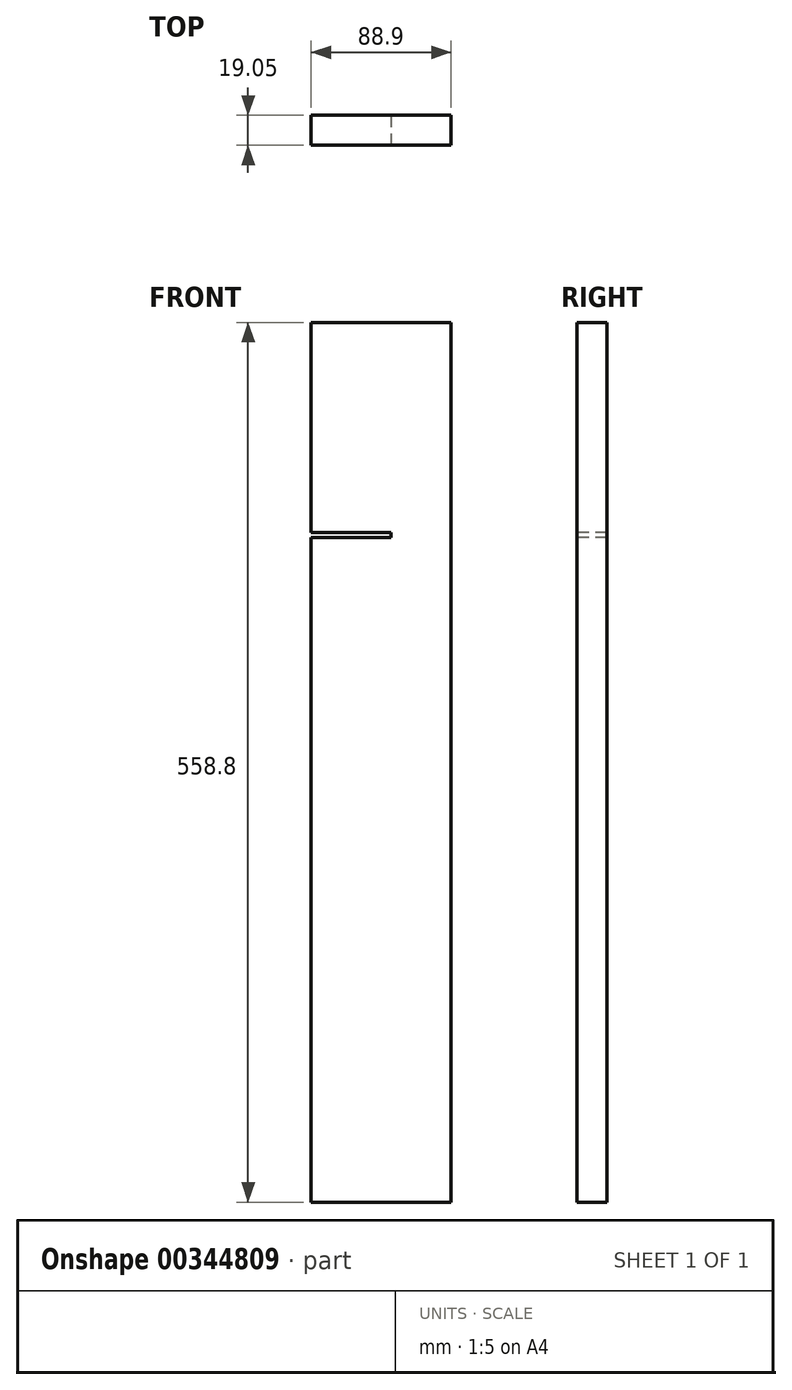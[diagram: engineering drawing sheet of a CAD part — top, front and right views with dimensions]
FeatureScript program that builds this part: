
annotation { "Feature Type Name" : "Feature", "Feature Type Description" : "" }
export const myFeature = defineFeature(function(context is Context, id is Id, definition is map)
    precondition{}
    {
        {
            var Q0;
            Q0=qCreatedBy(makeId("Front.planeOp"),FACE);
            var sketch = newSketch(context, id + "F0", { "sketchPlane" : qUnion([Q0])});
            skLineSegment(sketch, "E0.bottom", {"start": v(0, 0) * mm, "end": v(88.9, 0) * mm});
            skLineSegment(sketch, "E0.top", {"start": v(0, 558.8) * mm, "end": v(88.9, 558.8) * mm});
            skLineSegment(sketch, "E0.left", {"start": v(0, 0) * mm, "end": v(0, 558.8) * mm});
            skLineSegment(sketch, "E0.right", {"start": v(88.9, 0) * mm, "end": v(88.9, 558.8) * mm});
            skSolve(sketch);
        }
        {
            var Q0;
            Q0=makeQuery(id+"F0.imprint","IMPRINT",FACE,{"disambiguationData":[TD([[makeQuery(id+"F0.imprint","IMPRINT",EDGE,{"derivedFrom":sQuery(id+"F0.wireOp",EDGE,"E0.bottom")}),1.0]])]});
            extrude(context, id + "F1", {"entities" : qUnion([Q0]), "depth" : 19.05 * mm});
        }
        {
            var Q0;
            Q0=makeQuery(id+"F1.opExtrude","CAP_FACE",FACE,{"disambiguationData":[OSD([sQuery(id+"F0.wireOp",EDGE,"E0.bottom"),sQuery(id+"F0.wireOp",EDGE,"E0.top"),sQuery(id+"F0.wireOp",EDGE,"E0.left"),sQuery(id+"F0.wireOp",EDGE,"E0.right")])],"isStart":false});
            var sketch = newSketch(context, id + "F2", { "sketchPlane" : qUnion([Q0])});
            skLineSegment(sketch, "E1", {"start": v(0, 422.28) * mm, "end": v(88.9, 422.28) * mm, "construction": true});
            skLineSegment(sketch, "E2.bottom", {"start": v(0, 422.28) * mm, "end": v(50.8, 422.28) * mm});
            skLineSegment(sketch, "E2.top", {"start": v(0, 425.45) * mm, "end": v(50.8, 425.45) * mm});
            skLineSegment(sketch, "E2.left", {"start": v(0, 422.28) * mm, "end": v(0, 425.45) * mm});
            skLineSegment(sketch, "E2.right", {"start": v(50.8, 422.28) * mm, "end": v(50.8, 425.45) * mm});
            skSolve(sketch);
        }
        {
            var Q0;
            Q0=makeQuery(id+"F2.imprint","IMPRINT",FACE,{"disambiguationData":[TD([[makeQuery(id+"F2.imprint","IMPRINT",EDGE,{"derivedFrom":sQuery(id+"F2.wireOp",EDGE,"E2.bottom")}),1.0]])]});
            extrude(context, id + "F3", {"entities" : qUnion([Q0]), "operationType" : NewBodyOperationType.REMOVE, "oppositeDirection" : true, "depth" : 25.4 * mm});
        }
    });
